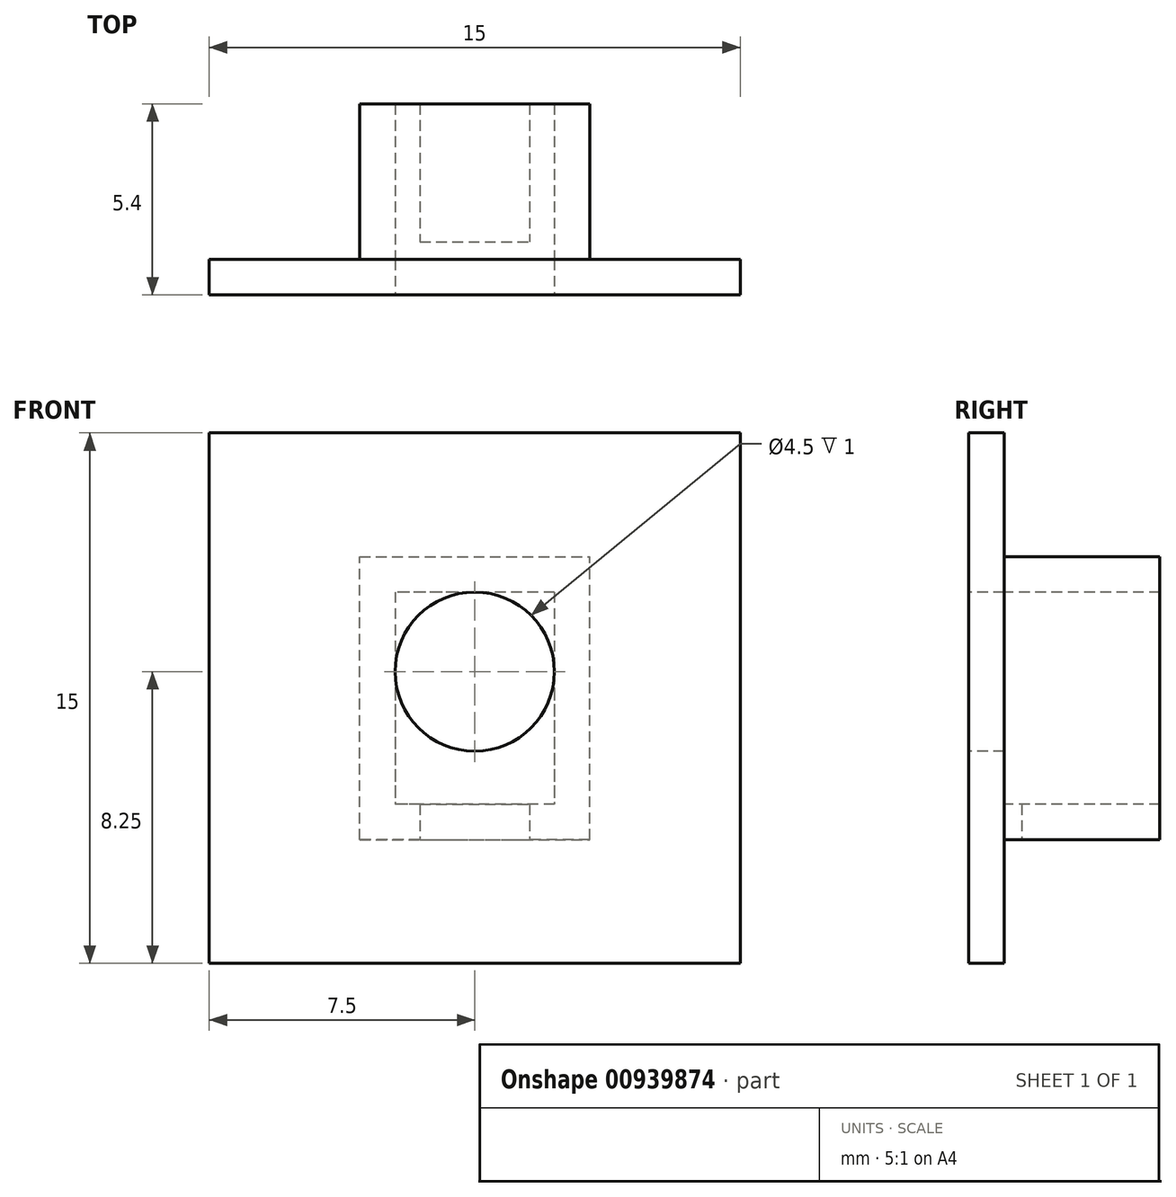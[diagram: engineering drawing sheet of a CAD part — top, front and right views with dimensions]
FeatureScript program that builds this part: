
annotation { "Feature Type Name" : "Feature", "Feature Type Description" : "" }
export const myFeature = defineFeature(function(context is Context, id is Id, definition is map)
    precondition{}
    {
        {
            var Q0;
            Q0=qCreatedBy(makeId("Front.planeOp"),FACE);
            var sketch = newSketch(context, id + "F0", { "sketchPlane" : qUnion([Q0])});
            skLineSegment(sketch, "E0.bottom", {"start": v(3.25, 4) * mm, "end": v(-3.25, 4) * mm});
            skLineSegment(sketch, "E0.top", {"start": v(3.25, -4) * mm, "end": v(-3.25, -4) * mm});
            skLineSegment(sketch, "E0.left", {"start": v(3.25, 4) * mm, "end": v(3.25, -4) * mm});
            skLineSegment(sketch, "E0.right", {"start": v(-3.25, 4) * mm, "end": v(-3.25, -4) * mm});
            skPoint(sketch, "E0.middle", {"position": v(0, 0) * mm});
            skSolve(sketch);
        }
        {
            var Q0;
            Q0 = qSketchRegion(id + "F0", true);
            extrude(context, id + "F1", {"entities" : qUnion([Q0]), "oppositeDirection" : true, "depth" : 5.4 * mm, "offsetDistance" : 25 * mm});
        }
        {
            var Q0;
            Q0=makeQuery(id+"F1.opExtrude","CAP_FACE",FACE,{"disambiguationData":[OSD([sQuery(id+"F0.wireOp",EDGE,"E0.bottom"),sQuery(id+"F0.wireOp",EDGE,"E0.top"),sQuery(id+"F0.wireOp",EDGE,"E0.left"),sQuery(id+"F0.wireOp",EDGE,"E0.right")])],"isStart":false});
            shell(context, id + "F2", {"entities" : qUnion([Q0]), "thickness" : 1 * mm});
        }
        {
            var Q0;
            Q0=makeQuery(id+"F1.opExtrude","SWEPT_FACE",FACE,{"disambiguationData":[OSD([sQuery(id+"F0.wireOp",EDGE,"E0.top")])]});
            var sketch = newSketch(context, id + "F3", { "sketchPlane" : qUnion([Q0])});
            skLineSegment(sketch, "E1.bottom", {"start": v(-1.55, -5.4) * mm, "end": v(1.55, -5.4) * mm});
            skLineSegment(sketch, "E1.top", {"start": v(-1.55, -1.5) * mm, "end": v(1.55, -1.5) * mm});
            skLineSegment(sketch, "E1.left", {"start": v(-1.55, -5.4) * mm, "end": v(-1.55, -1.5) * mm});
            skLineSegment(sketch, "E1.right", {"start": v(1.55, -5.4) * mm, "end": v(1.55, -1.5) * mm});
            skSolve(sketch);
        }
        {
            var Q0;
            Q0 = qSketchRegion(id + "F3", true);
            extrude(context, id + "F4", {"entities" : qUnion([Q0]), "operationType" : NewBodyOperationType.REMOVE, "oppositeDirection" : true, "depth" : 1 * mm, "offsetDistance" : 25 * mm});
        }
        {
            var Q0;
            Q0=makeQuery(id+"F1.opExtrude","CAP_FACE",FACE,{"disambiguationData":[OSD([sQuery(id+"F0.wireOp",EDGE,"E0.bottom"),sQuery(id+"F0.wireOp",EDGE,"E0.top"),sQuery(id+"F0.wireOp",EDGE,"E0.left"),sQuery(id+"F0.wireOp",EDGE,"E0.right")])],"isStart":true});
            var sketch = newSketch(context, id + "F5", { "sketchPlane" : qUnion([Q0])});
            skLineSegment(sketch, "E2.bottom", {"start": v(-7.5, 7.5) * mm, "end": v(7.5, 7.5) * mm});
            skLineSegment(sketch, "E2.top", {"start": v(-7.5, -7.5) * mm, "end": v(7.5, -7.5) * mm});
            skLineSegment(sketch, "E2.left", {"start": v(-7.5, 7.5) * mm, "end": v(-7.5, -7.5) * mm});
            skLineSegment(sketch, "E2.right", {"start": v(7.5, 7.5) * mm, "end": v(7.5, -7.5) * mm});
            skPoint(sketch, "E2.middle", {"position": v(0, 0) * mm});
            skSolve(sketch);
        }
        {
            var Q0;
            Q0 = qSketchRegion(id + "F5", true);
            extrude(context, id + "F6", {"entities" : qUnion([Q0]), "operationType" : NewBodyOperationType.ADD, "oppositeDirection" : true, "depth" : 1 * mm, "offsetDistance" : 25 * mm});
        }
        {
            var Q0;
            Q0=makeQuery(id+"F6.boolean.opBoolean","MERGE",FACE,{"derivedFrom":[makeQuery(id+"F1.opExtrude","CAP_FACE",FACE,{"disambiguationData":[OSD([sQuery(id+"F0.wireOp",EDGE,"E0.bottom"),sQuery(id+"F0.wireOp",EDGE,"E0.top"),sQuery(id+"F0.wireOp",EDGE,"E0.left"),sQuery(id+"F0.wireOp",EDGE,"E0.right")])],"isStart":true}),makeQuery(id+"F6.opExtrude","CAP_FACE",FACE,{"disambiguationData":[OSD([sQuery(id+"F5.wireOp",EDGE,"E2.bottom"),sQuery(id+"F5.wireOp",EDGE,"E2.top"),sQuery(id+"F5.wireOp",EDGE,"E2.left"),sQuery(id+"F5.wireOp",EDGE,"E2.right")])],"isStart":true})]});
            var sketch = newSketch(context, id + "F7", { "sketchPlane" : qUnion([Q0])});
            skCircle(sketch, "E3", {"center": v(0, 0.75) * mm, "radius": 2.25 * mm});
            skSolve(sketch);
        }
        {
            var Q0;
            Q0 = qSketchRegion(id + "F7", true);
            extrude(context, id + "F8", {"entities" : qUnion([Q0]), "operationType" : NewBodyOperationType.REMOVE, "oppositeDirection" : true, "depth" : 25 * mm, "offsetDistance" : 25 * mm});
        }
    });
